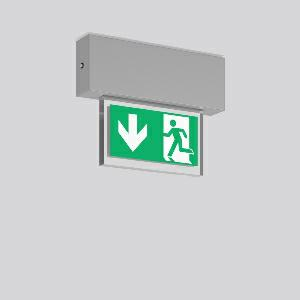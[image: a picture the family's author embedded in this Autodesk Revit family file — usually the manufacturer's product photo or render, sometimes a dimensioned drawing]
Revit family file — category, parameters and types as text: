
# Revit family: halyxx_671504_004_1_30d6
name_source: partatom
category: Lighting Fixtures
units: mm (PartAtom-declared; Revit-internal decimal feet)

## family parameters
Cut with Voids When Loaded = No
Host = Face
Light Source = No
Part Type = Normal
Room Calculation Point = No
Round Connector Dimension = Use Diameter
Shared = No

## types (1)
- HALYXX (1 x LED Modul 840, 45 lm, 4000)
    Apparent Load = 2 VA
    Approval mark = CE
    CIE Flux Codes = 18 46 75 53 100
    Color Rendering = 80
    Color Temperature = 4000
    Default Elevation = 1800 mm
    Description = Series: HALYXX
Luminaire for escape route identification. Housing: extruded aluminium profile, anodised or powder-coated. Display panel: highly transparent panel, plastic, with legend on one side/both sides. Driver integrated. Suitable for connection to central battery systems. Please indicate legend number when placing your order! 
Colour: anodised aluminium
Length: 233 mm
Width: 40 mm
Height: 184 mm
Weight: 0.98 kg
Operating mode: maintained power mode
Viewing Distance: 14 m
Lamp: LED
Socket: without socket
Colour temperature: 4000K
Colour rendering index (CRI): 80
System power: 2 W
Rated luminous flux: 45 lm
Luminous flux, emergency: 45
System power, emergency: 1.8 W
Control gear: Regulated power supply
Protection class: I
Type of protection: IP 40
    Height = 184 mm
    Lamp = 1 x LED Modul 840
    Lamp Light Flux = 45 lm
    Lamp count = 1
    Length = 233 mm
    Lifetime = 50000 h
    Luminous efficacy = 23 lm/W
    Manufacturer = RZB
    ModVariant = No
    Model = 671504.004.1
    Mounting Place = Ceiling
    Mounting Type = Surface mounted
    Number of Poles = 1
    OnlyDefault = Yes
    Power Factor = 1
    Product Name = HALYXX
    Product group = Surface mounted ceiling luminaires
    ProductGroupID = 303
    Protection Class = Protection class I
    Protection Degree = IP 40
    RLX_Detail_Level = 1
    RLX_Emergency_Light_Flux = 45 lm
    RLX_Emergency_Type = 3
    RLX_Emergency_Type_DB = Yes
    RlxData = <blob elided: 36553 chars, md5=72567417>
    Socket = socket
    Standby Power = 0 W
    System Light Flux = 45 lm
    System Power = 2 W
    Type Comments = Product without accessories
    Type Image = 671502.004.jpg
    URL = http://relux.com
    VarID = ---
    Voltage = 230 V
    Voltage Range = 220-240 V
    Weight = 0.00 kg
    Width = 40 mm  [stored 0.131234 ft]

note: [stored X ft] marks values corroborated as IEEE doubles in the binary element streams (Revit-internal decimal feet)

## geometry (parser evidence)
native form markers: Blend x4, Sweep x15
no freeform markers — native parametric forms only
